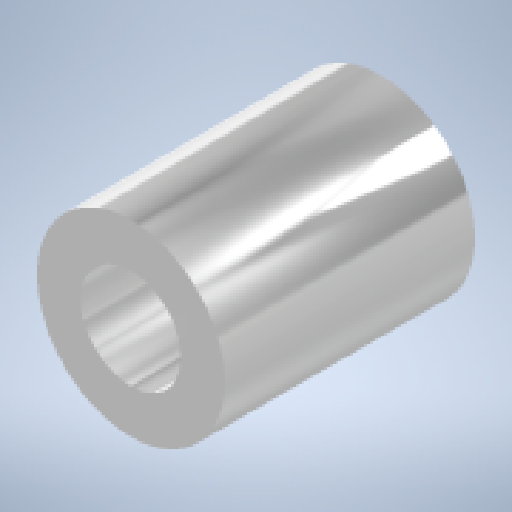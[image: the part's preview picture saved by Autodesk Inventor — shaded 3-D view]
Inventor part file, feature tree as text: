
AUTODESK INVENTOR PART (.ipt)
format: ipt  version: 2024 (Build 280153000, 153)  size: 139,776 bytes
history: native  units: mm
features: other x1, extrude x1, sketch x1
ambient origin geometry x8: Origin, YZ Plane, XZ Plane, XY Plane, X Axis, Y Axis, Z Axis, Center Point
bodies: Body1 (feature_tree)
feature tree (3):
  other  "ソリッド1"
  extrude  "押し出し1"  Depth=3.2mm
  sketch  "スケッチ1"
